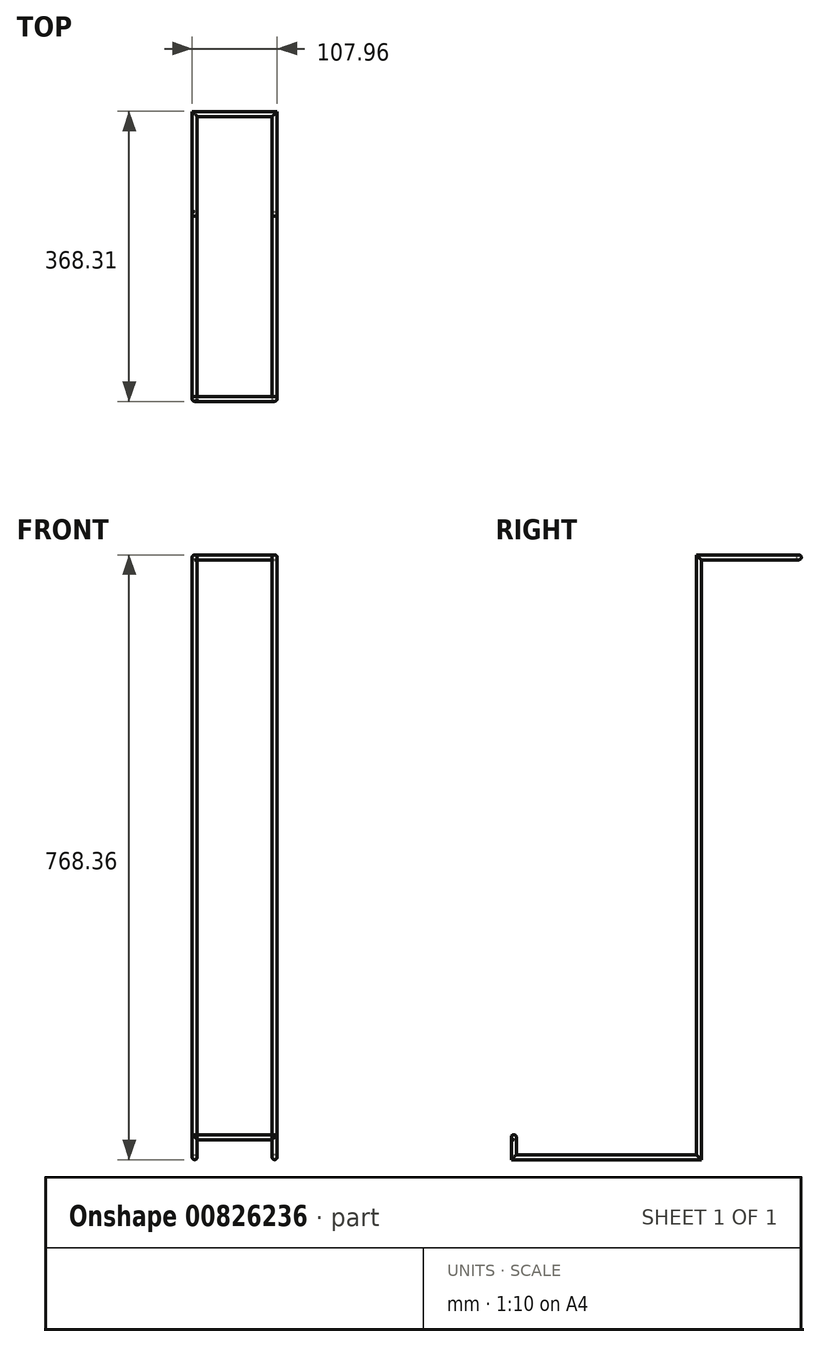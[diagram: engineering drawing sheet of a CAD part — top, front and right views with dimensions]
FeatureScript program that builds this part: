
annotation { "Feature Type Name" : "Feature", "Feature Type Description" : "" }
export const myFeature = defineFeature(function(context is Context, id is Id, definition is map)
    precondition{}
    {
        {
            var Q0;
            Q0=qCreatedBy(makeId("Front.planeOp"),FACE);
            var sketch = newSketch(context, id + "F0", { "sketchPlane" : qUnion([Q0])});
            skCircle(sketch, "E0", {"center": v(0, 0) * mm, "radius": 3.18 * mm});
            skSolve(sketch);
        }
        {
            var Q0;
            Q0=qCreatedBy(makeId("Top.planeOp"),FACE);
            var sketch = newSketch(context, id + "F1", { "sketchPlane" : qUnion([Q0])});
            skPoint(sketch, "E1.0", {"position": v(0, 0) * mm});
            skLineSegment(sketch, "E2", {"start": v(0, 0) * mm, "end": v(0, 127) * mm});
            skLineSegment(sketch, "E3", {"start": v(0, 127) * mm, "end": v(101.6, 127) * mm});
            skLineSegment(sketch, "E4", {"start": v(101.6, 127) * mm, "end": v(101.6, 0) * mm});
            skSolve(sketch);
        }
        {
            var Q0;
            Q0=qCreatedBy(makeId("Front.planeOp"),FACE);
            var sketch = newSketch(context, id + "F2", { "sketchPlane" : qUnion([Q0])});
            skPoint(sketch, "E5.0", {"position": v(101.6, 0) * mm});
            skLineSegment(sketch, "E6", {"start": v(101.6, 0) * mm, "end": v(101.6, -762) * mm});
            skLineSegment(sketch, "E7", {"start": v(0, 0) * mm, "end": v(0, -762) * mm});
            skSolve(sketch);
        }
        {
            var Q0;
            Q0=qCreatedBy(makeId("Top.planeOp"),FACE);
            cPlane(context, id + "F3", {"entities" : qUnion([Q0]), "cplaneType" : CPlaneType.OFFSET, "offset" : 762 * mm, "oppositeDirection" : true, "width" : 152.4 * mm, "height" : 152.4 * mm});
        }
        {
            var Q0;
            Q0=qCreatedBy(id+"F3.planeOp",FACE);
            var sketch = newSketch(context, id + "F4", { "sketchPlane" : qUnion([Q0])});
            skPoint(sketch, "E8.0", {"position": v(0, 0) * mm});
            skLineSegment(sketch, "E9", {"start": v(0, 0) * mm, "end": v(0, -234.95) * mm});
            skLineSegment(sketch, "E10", {"start": v(101.6, -234.95) * mm, "end": v(101.6, 0) * mm});
            skSolve(sketch);
        }
        {
            var Q0;
            Q0=sQuery(id+"F4.wireOp",VERTEX,"E9.end");
            var Q1;
            Q1=qCreatedBy(makeId("Front.planeOp"),FACE);
            cPlane(context, id + "F5", {"entities" : qUnion([Q0, Q1]), "cplaneType" : CPlaneType.PLANE_POINT, "offset" : 25.4 * mm, "width" : 152.4 * mm, "height" : 152.4 * mm});
        }
        {
            var Q0;
            Q0=qCreatedBy(id+"F5.planeOp",FACE);
            var sketch = newSketch(context, id + "F6", { "sketchPlane" : qUnion([Q0])});
            skPoint(sketch, "E11.0", {"position": v(0, -762) * mm});
            skLineSegment(sketch, "E12", {"start": v(0, -762) * mm, "end": v(0, -736.6) * mm});
            skLineSegment(sketch, "E13", {"start": v(0, -736.6) * mm, "end": v(101.6, -736.6) * mm});
            skPoint(sketch, "E14.0", {"position": v(101.6, -762) * mm});
            skLineSegment(sketch, "E15", {"start": v(101.6, -736.6) * mm, "end": v(101.6, -762) * mm});
            skSolve(sketch);
        }
        {
            var Q0;
            Q0=makeQuery(id+"F0.imprint","IMPRINT",FACE,{"disambiguationData":[TD([[makeQuery(id+"F0.imprint","IMPRINT",EDGE,{"derivedFrom":sQuery(id+"F0.wireOp",EDGE,"E0")}),1.0]])]});
            var Q1;
            Q1=sQuery(id+"F1.wireOp",EDGE,"E2");
            var Q2;
            Q2=sQuery(id+"F1.wireOp",EDGE,"E3");
            var Q3;
            Q3=sQuery(id+"F1.wireOp",EDGE,"E4");
            var Q4;
            Q4=sQuery(id+"F2.wireOp",EDGE,"E6");
            var Q5;
            Q5=sQuery(id+"F4.wireOp",EDGE,"E10");
            var Q6;
            Q6=sQuery(id+"F6.wireOp",EDGE,"E15");
            var Q7;
            Q7=sQuery(id+"F6.wireOp",EDGE,"E13");
            var Q8;
            Q8=sQuery(id+"F6.wireOp",EDGE,"E12");
            var Q9;
            Q9=sQuery(id+"F4.wireOp",EDGE,"E9");
            var Q10;
            Q10=sQuery(id+"F2.wireOp",EDGE,"E7");
            sweep(context, id + "F7", {"profiles" : qUnion([Q0]), "path" : qUnion([Q1, Q2, Q3, Q4, Q5, Q6, Q7, Q8, Q9, Q10])});
        }
        {
            var Q0;
            Q0=sQuery(id+"F4.wireOp",EDGE,"E9");
            cPlane(context, id + "F8", {"entities" : qUnion([Q0]), "cplaneType" : CPlaneType.LINE_ANGLE, "offset" : 25.4 * mm, "angle" : 90 * degree, "width" : 152.4 * mm, "height" : 152.4 * mm});
        }
        {
            var Q0;
            Q0=qCreatedBy(id+"F8.planeOp",FACE);
            var sketch = newSketch(context, id + "F9", { "sketchPlane" : qUnion([Q0])});
            skPoint(sketch, "E16.0", {"position": v(0, -762) * mm});
            skLineSegment(sketch, "E17", {"start": v(0, -762) * mm, "end": v(0, -723.9) * mm});
            skLineSegment(sketch, "E18", {"start": v(0, -762) * mm, "end": v(-38.1, -762) * mm});
            skArc(sketch, "E19", {"start": v(-38.1, -762) * mm, "mid": v(26.94, -788.94) * mm, "end": v(0, -723.9) * mm});
            skSolve(sketch);
        }
        {
            var Q0;
            Q0=sQuery(id+"F9.wireOp",EDGE,"E17");
            cPlane(context, id + "F10", {"entities" : qUnion([Q0]), "cplaneType" : CPlaneType.LINE_ANGLE, "offset" : 25.4 * mm, "angle" : 90 * degree, "width" : 152.4 * mm, "height" : 152.4 * mm});
        }
    });
